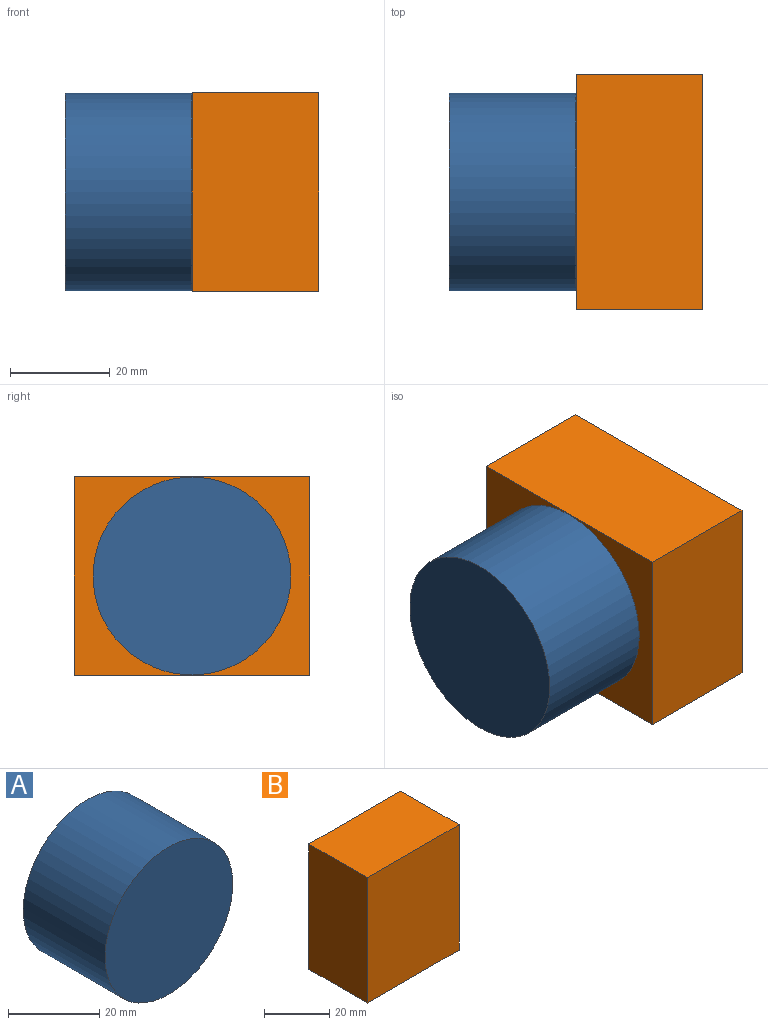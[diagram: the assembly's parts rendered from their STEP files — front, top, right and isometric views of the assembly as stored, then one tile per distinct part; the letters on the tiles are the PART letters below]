
ASSEMBLY  parts=2 mates=1
PART A: 3 faces, bbox 39.7x25.4x39.7 mm
  f0: cylinder r=19.84mm len=39.67mm, axis (0,1,0), area 3165.6mm2, adj f1,f2
  f1: plane 39.67x39.67mm, normal (0,-1,0), area 1236.1mm2, adj f0
  f2: plane 39.67x39.67mm, normal (0,1,0), area 1236.1mm2, adj f0
PART B: 6 faces, bbox 39.9x25.4x47.2 mm
  f0: plane 39.9x25.4mm, normal (0,0,1), area 1013.4mm2, adj f1,f3,f4,f5
  f1: plane 47.17x25.4mm, normal (-1,0,0), area 1198.2mm2, adj f0,f2,f4,f5
  f2: plane 39.9x25.4mm, normal (0,0,-1), area 1013.4mm2, adj f1,f3,f4,f5
  f3: plane 47.17x25.4mm, normal (1,0,0), area 1198.2mm2, adj f0,f2,f4,f5
  f4: plane 47.17x39.9mm, normal (0,-1,0), area 1882.1mm2, adj f0,f1,f2,f3
  f5: plane 47.17x39.9mm, normal (0,1,0), area 1882.1mm2, adj f0,f1,f2,f3
PLACE A rot(axis=(-0.58,0.58,0.58),120deg) t=(-50.8,0,0)mm
PLACE B rot(axis=(0.58,0.58,-0.58),120deg) t=(25.4,-23.59,19.95)mm
MATE fastened A.f0 <-> B.f4  axis (1,0,0) through (-25.4,0,0)mm
